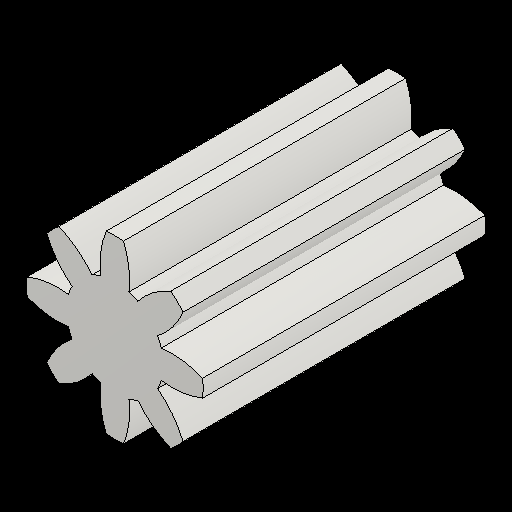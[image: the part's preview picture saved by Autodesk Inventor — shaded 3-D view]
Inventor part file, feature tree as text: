
AUTODESK INVENTOR PART (.ipt)
format: ipt  version: 2023.2 (Build 272271030, 271C)  size: 179,200 bytes
history: native  units: mm (DEFAULTED — no unit token found)
features: plane x3, other x3, sketch x2, extrude x1
ambient origin geometry x8: Origin, YZ Plane, XZ Plane, XY Plane, X Axis, Y Axis, Z Axis, Center Point
bodies: Solid1 (feature_tree)
feature tree (9):
  extrude  "Extrusion1"  Depth=20.0mm TaperAngle=0.0deg
  plane  "Work Plane2"
  plane  "Work Plane8"
  plane  "Work Plane9"
  other  "Spur Gear"
  sketch  "Sketch1"  dims[d0=12.5mm d1=20.0mm d2=0.0mm]
  sketch  "Sketch2"  dims[d3=10.0mm d4=10.0mm d5=0.0mm d16=10.0mm d17=0.0mm d34=22.5deg d39=0.0mm d41=0.0mm d43=10.0mm d46=10.0mm d47=0.0mm d48=0.0mm]
  other  "Srf1"
  other  "Pitch Diameter"
